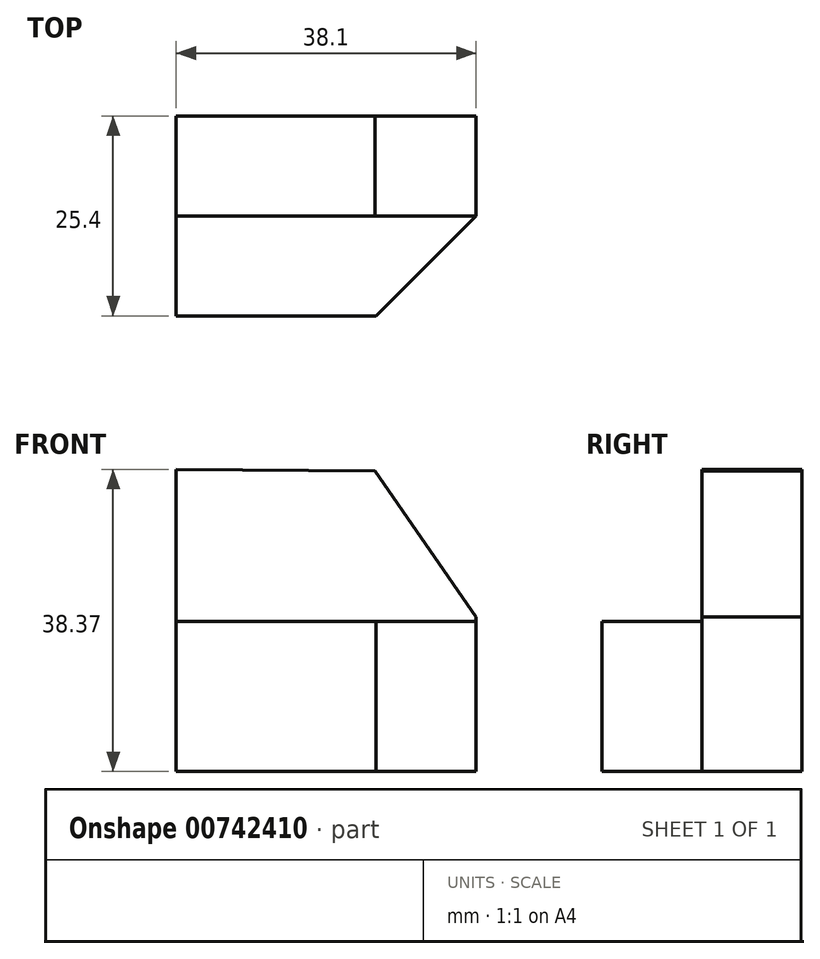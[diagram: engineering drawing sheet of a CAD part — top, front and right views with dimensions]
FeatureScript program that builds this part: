
annotation { "Feature Type Name" : "Feature", "Feature Type Description" : "" }
export const myFeature = defineFeature(function(context is Context, id is Id, definition is map)
    precondition{}
    {
        {
            var Q0;
            Q0=qCreatedBy(makeId("Front.planeOp"),FACE);
            var sketch = newSketch(context, id + "F0", { "sketchPlane" : qUnion([Q0])});
            skLineSegment(sketch, "E0", {"start": v(0, 38.37) * mm, "end": v(0, 0) * mm});
            skLineSegment(sketch, "E1", {"start": v(0, 0) * mm, "end": v(38.1, 0) * mm});
            skLineSegment(sketch, "E2", {"start": v(38.1, 0) * mm, "end": v(38.1, 38.1) * mm});
            skLineSegment(sketch, "E3", {"start": v(38.1, 38.1) * mm, "end": v(0, 38.37) * mm});
            skSolve(sketch);
        }
        {
            var Q0;
            Q0 = qSketchRegion(id + "F0", true);
            extrude(context, id + "F1", {"entities" : qUnion([Q0]), "depth" : 25.4 * mm, "offsetDistance" : 25.4 * mm});
        }
        {
            var Q0;
            Q0=qCreatedBy(makeId("Right.planeOp"),FACE);
            var sketch = newSketch(context, id + "F2", { "sketchPlane" : qUnion([Q0])});
            skLineSegment(sketch, "E4", {"start": v(-12.7, 38.49) * mm, "end": v(-12.7, 19.05) * mm});
            skLineSegment(sketch, "E5", {"start": v(-12.7, 19.05) * mm, "end": v(-25.45, 19.05) * mm});
            skLineSegment(sketch, "E6", {"start": v(-12.7, 38.49) * mm, "end": v(-25.47, 38.49) * mm});
            skLineSegment(sketch, "E7", {"start": v(-25.47, 38.49) * mm, "end": v(-25.45, 19.05) * mm});
            skSolve(sketch);
        }
        {
            var Q0;
            Q0 = qSketchRegion(id + "F2", true);
            extrude(context, id + "F3", {"entities" : qUnion([Q0]), "operationType" : NewBodyOperationType.REMOVE, "endBound" : BoundingType.THROUGH_ALL, "depth" : 25.4 * mm, "offsetDistance" : 25.4 * mm});
        }
        {
            var Q0;
            Q0=qCreatedBy(makeId("Front.planeOp"),FACE);
            var sketch = newSketch(context, id + "F4", { "sketchPlane" : qUnion([Q0])});
            skLineSegment(sketch, "E8", {"start": v(25.07, 38.42) * mm, "end": v(38.13, 19.6) * mm});
            skLineSegment(sketch, "E9", {"start": v(38.13, 19.6) * mm, "end": v(38.13, 38.23) * mm});
            skLineSegment(sketch, "E10", {"start": v(38.13, 38.23) * mm, "end": v(25.07, 38.42) * mm});
            skSolve(sketch);
        }
        {
            var Q0;
            Q0 = qSketchRegion(id + "F4", true);
            extrude(context, id + "F5", {"entities" : qUnion([Q0]), "operationType" : NewBodyOperationType.REMOVE, "endBound" : BoundingType.THROUGH_ALL, "depth" : 25.4 * mm, "offsetDistance" : 25.4 * mm});
        }
        {
            var Q0;
            Q0=makeQuery(id+"F3.boolean.opBoolean","COPY",FACE,{"derivedFrom":makeQuery(id+"F3.opExtrude","SWEPT_FACE",FACE,{"disambiguationData":[OSD([sQuery(id+"F2.wireOp",EDGE,"E5")])]})});
            var sketch = newSketch(context, id + "F6", { "sketchPlane" : qUnion([Q0])});
            skLineSegment(sketch, "E11", {"start": v(38.1, -12.7) * mm, "end": v(25.4, -25.4) * mm});
            skSolve(sketch);
        }
        {
            var Q0;
            Q0 = qSketchRegion(id + "F6", true);
            var Q1;
            {var subQ0=sQuery(id+"F6.wireOp",EDGE,"E11");Q1=makeQuery(id+"F6.imprint","IMPRINT",FACE,{"disambiguationData":[TD([[makeQuery(id+"F6.imprint","IMPRINT",EDGE,{"derivedFrom":subQ0}),1.0]])]});}
            extrude(context, id + "F7", {"entities" : qUnion([Q0, Q1]), "operationType" : NewBodyOperationType.REMOVE, "endBound" : BoundingType.THROUGH_ALL, "oppositeDirection" : true, "depth" : 25.4 * mm, "offsetDistance" : 25.4 * mm});
        }
    });
